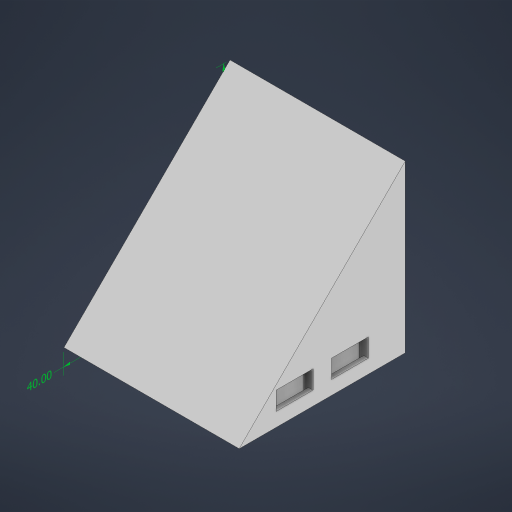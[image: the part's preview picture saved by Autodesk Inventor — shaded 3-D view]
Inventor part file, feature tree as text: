
AUTODESK INVENTOR PART (.ipt)
format: ipt  version: 2024 (Build 280153000, 153)  size: 233,984 bytes
history: native  units: mm
features: other x6, extrude x5, sketch x5
ambient origin geometry x8: Origin, YZ Plane, XZ Plane, XY Plane, X Axis, Y Axis, Z Axis, Center Point
bodies: Body1 (feature_tree)
feature tree (16):
  other  "솔리드1"
  extrude  "돌출1"  Depth=180.0mm
  extrude  "돌출2"  Depth=180.0mm
  extrude  "돌출3"  Depth=190.0mm TaperAngle=0.0deg
  extrude  "돌출4"  Depth=40.0mm
  extrude  "돌출5"  Depth=20.0mm
  sketch  "스케치1"
  sketch  "스케치2"
  sketch  "스케치3"
  sketch  "스케치4"
  sketch  "스케치5"
  other  "선형 치수 1"
  other  "선형 치수 2"
  other  "선형 치수 3"
  other  "선형 치수 4"
  other  "선형 치수 5"
